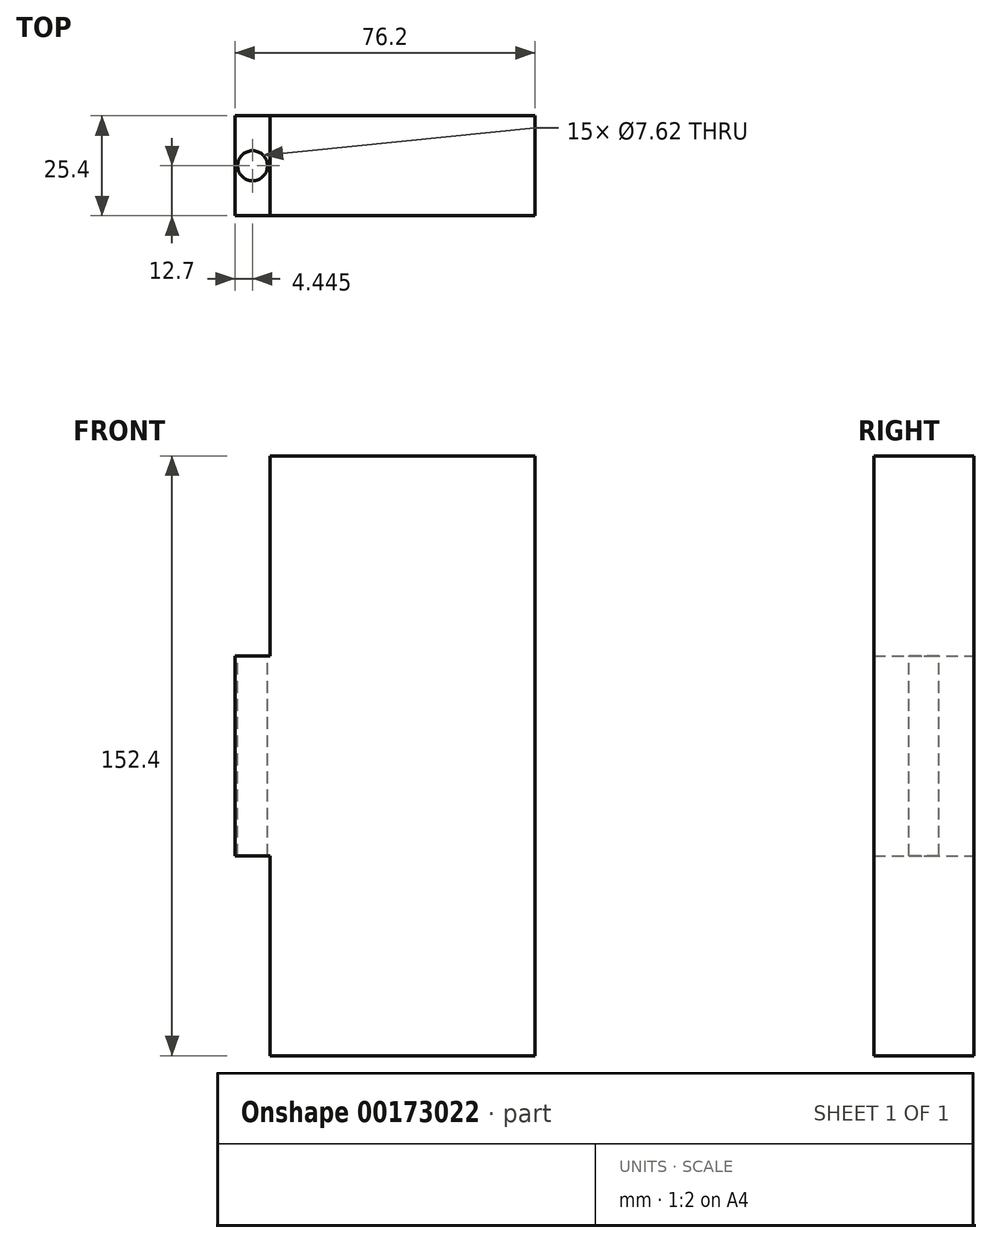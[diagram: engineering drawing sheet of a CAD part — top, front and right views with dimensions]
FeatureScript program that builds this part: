
annotation { "Feature Type Name" : "Feature", "Feature Type Description" : "" }
export const myFeature = defineFeature(function(context is Context, id is Id, definition is map)
    precondition{}
    {
        {
            var Q0;
            Q0=qCreatedBy(makeId("Front.planeOp"),FACE);
            var sketch = newSketch(context, id + "F0", { "sketchPlane" : qUnion([Q0])});
            skPoint(sketch, "E0.middle", {"position": v(0, 0) * mm});
            skLineSegment(sketch, "E1", {"start": v(0, 0) * mm, "end": v(0, 25.4) * mm});
            skLineSegment(sketch, "E2", {"start": v(0, 0) * mm, "end": v(0, -25.4) * mm});
            skLineSegment(sketch, "E3", {"start": v(0, 25.4) * mm, "end": v(8.9, 25.4) * mm});
            skLineSegment(sketch, "E4", {"start": v(0, -25.4) * mm, "end": v(8.9, -25.4) * mm});
            skLineSegment(sketch, "E5", {"start": v(8.9, 25.4) * mm, "end": v(8.9, 76.2) * mm});
            skLineSegment(sketch, "E6", {"start": v(8.9, -25.4) * mm, "end": v(8.9, -76.2) * mm});
            skLineSegment(sketch, "E7", {"start": v(8.9, 76.2) * mm, "end": v(76.2, 76.2) * mm});
            skLineSegment(sketch, "E8", {"start": v(8.9, -76.2) * mm, "end": v(76.2, -76.2) * mm});
            skLineSegment(sketch, "E9", {"start": v(76.2, 76.2) * mm, "end": v(76.2, -76.2) * mm});
            skSolve(sketch);
        }
        {
            var Q0;
            Q0=makeQuery(id+"F0.imprint","IMPRINT",FACE,{"disambiguationData":[TD([[makeQuery(id+"F0.imprint","IMPRINT",EDGE,{"derivedFrom":sQuery(id+"F0.wireOp",EDGE,"E1")}),-1.0]])]});
            extrude(context, id + "F1", {"entities" : qUnion([Q0]), "depth" : 25.4 * mm});
        }
        {
            var Q0;
            Q0=makeQuery(id+"F1.opExtrude","SWEPT_FACE",FACE,{"disambiguationData":[OSD([sQuery(id+"F0.wireOp",EDGE,"E3")])]});
            var sketch = newSketch(context, id + "F2", { "sketchPlane" : qUnion([Q0])});
            skLineSegment(sketch, "E10", {"start": v(0, 0) * mm, "end": v(4.45, 0) * mm});
            skLineSegment(sketch, "E11", {"start": v(4.45, 0) * mm, "end": v(4.45, -12.7) * mm});
            skPoint(sketch, "E11.endSnap0", {"position": v(4.45, -25.4) * mm});
            skCircle(sketch, "E12", {"center": v(4.45, -12.7) * mm, "radius": 3.81 * mm});
            skSolve(sketch);
        }
        {
            var Q0;
            Q0=makeQuery(id+"F2.imprint","IMPRINT",FACE,{"disambiguationData":[TD([[makeQuery(id+"F2.imprint","IMPRINT",EDGE,{"derivedFrom":sQuery(id+"F2.wireOp",EDGE,"E12")}),1.0]])]});
            var Q1;
            Q1=sQuery(id+"F2.wireOp",EDGE,"E12");
            extrude(context, id + "F3", {"entities" : qUnion([Q0]), "operationType" : NewBodyOperationType.REMOVE, "surfaceEntities" : qUnion([Q1]), "endBound" : BoundingType.THROUGH_ALL, "oppositeDirection" : true, "depth" : 25.4 * mm});
        }
    });
